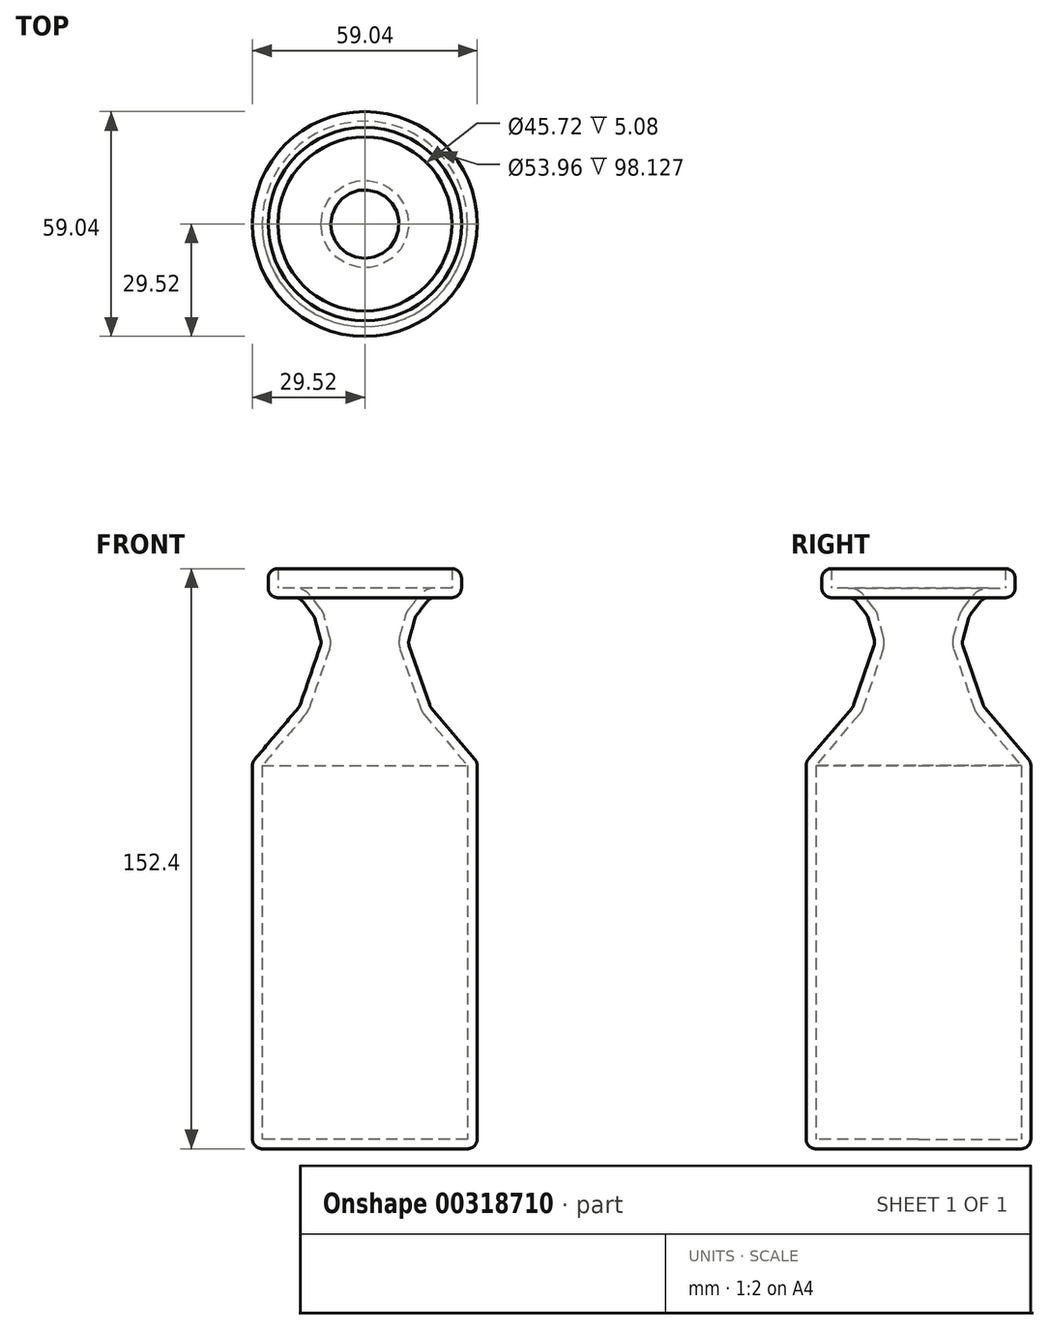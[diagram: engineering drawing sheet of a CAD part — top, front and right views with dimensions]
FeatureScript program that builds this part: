
annotation { "Feature Type Name" : "Feature", "Feature Type Description" : "" }
export const myFeature = defineFeature(function(context is Context, id is Id, definition is map)
    precondition{}
    {
        {
            var Q0;
            Q0=qCreatedBy(makeId("Front.planeOp"),FACE);
            var sketch = newSketch(context, id + "F0", { "sketchPlane" : qUnion([Q0])});
            skLineSegment(sketch, "E0", {"start": v(0, 62.47) * mm, "end": v(-25.4, 62.47) * mm});
            skLineSegment(sketch, "E1", {"start": v(-25.4, 62.47) * mm, "end": v(-25.4, 54.85) * mm});
            skLineSegment(sketch, "E2", {"start": v(-25.4, 54.85) * mm, "end": v(-17.16, 54.85) * mm});
            skLineSegment(sketch, "E3", {"start": v(-17.16, 54.85) * mm, "end": v(-13.32, 49.9) * mm});
            skLineSegment(sketch, "E4", {"start": v(-13.32, 49.9) * mm, "end": v(-11.4, 42.97) * mm});
            skLineSegment(sketch, "E5", {"start": v(-11.4, 42.97) * mm, "end": v(-17.16, 26.22) * mm});
            skLineSegment(sketch, "E6", {"start": v(-17.16, 26.22) * mm, "end": v(-29.52, 11.67) * mm});
            skLineSegment(sketch, "E7", {"start": v(-29.52, 11.67) * mm, "end": v(-29.52, -89.93) * mm});
            skLineSegment(sketch, "E8", {"start": v(-29.52, -89.93) * mm, "end": v(0, -89.93) * mm});
            skLineSegment(sketch, "E9", {"start": v(0, -89.93) * mm, "end": v(0, 62.47) * mm});
            skSolve(sketch);
        }
        {
            var Q0;
            Q0=makeQuery(id+"F0.imprint","IMPRINT",FACE,{"disambiguationData":[TD([[makeQuery(id+"F0.imprint","IMPRINT",EDGE,{"derivedFrom":sQuery(id+"F0.wireOp",EDGE,"E0")}),1.0]])]});
            var Q1;
            Q1=sQuery(id+"F0.wireOp",EDGE,"E9");
            revolve(context, id + "F1", {"entities" : qUnion([Q0]), "axis" : qUnion([Q1]), "revolveType" : RevolveType.FULL});
        }
        {
            var Q0;
            Q0=makeQuery(id+"F1.opRevolve","SWEPT_EDGE",EDGE,{"disambiguationData":[OSD([sQuery(id+"F0.wireOp",EDGE,"E0"),sQuery(id+"F0.wireOp",EDGE,"E1")])]});
            var Q1;
            Q1=makeQuery(id+"F1.opRevolve","SWEPT_EDGE",EDGE,{"disambiguationData":[OSD([sQuery(id+"F0.wireOp",EDGE,"E1"),sQuery(id+"F0.wireOp",EDGE,"E2")])]});
            var Q2;
            Q2=makeQuery(id+"F1.opRevolve","SWEPT_EDGE",EDGE,{"disambiguationData":[OSD([sQuery(id+"F0.wireOp",EDGE,"E3"),sQuery(id+"F0.wireOp",EDGE,"E4")])]});
            var Q3;
            Q3=makeQuery(id+"F1.opRevolve","SWEPT_FACE",FACE,{"disambiguationData":[OSD([sQuery(id+"F0.wireOp",EDGE,"E3")])]});
            var Q4;
            Q4=makeQuery(id+"F1.opRevolve","SWEPT_FACE",FACE,{"disambiguationData":[OSD([sQuery(id+"F0.wireOp",EDGE,"E4")])]});
            var Q5;
            Q5=makeQuery(id+"F1.opRevolve","SWEPT_FACE",FACE,{"disambiguationData":[OSD([sQuery(id+"F0.wireOp",EDGE,"E5")])]});
            var Q6;
            Q6=makeQuery(id+"F1.opRevolve","SWEPT_FACE",FACE,{"disambiguationData":[OSD([sQuery(id+"F0.wireOp",EDGE,"E6")])]});
            var Q7;
            Q7=makeQuery(id+"F1.opRevolve","SWEPT_FACE",FACE,{"disambiguationData":[OSD([sQuery(id+"F0.wireOp",EDGE,"E7")])]});
            fillet(context, id + "F2", {"entities" : qUnion([Q0, Q1, Q2, Q3, Q4, Q5, Q6, Q7]), "radius" : 2.54 * mm, "tangentPropagation" : true, "allowEdgeOverflow" : false});
        }
        {
            var Q0;
            Q0=makeQuery(id+"F1.opRevolve","SWEPT_FACE",FACE,{"disambiguationData":[OSD([sQuery(id+"F0.wireOp",EDGE,"E0")])]});
            shell(context, id + "F3", {"entities" : qUnion([Q0]), "thickness" : 2.54 * mm});
        }
    });
